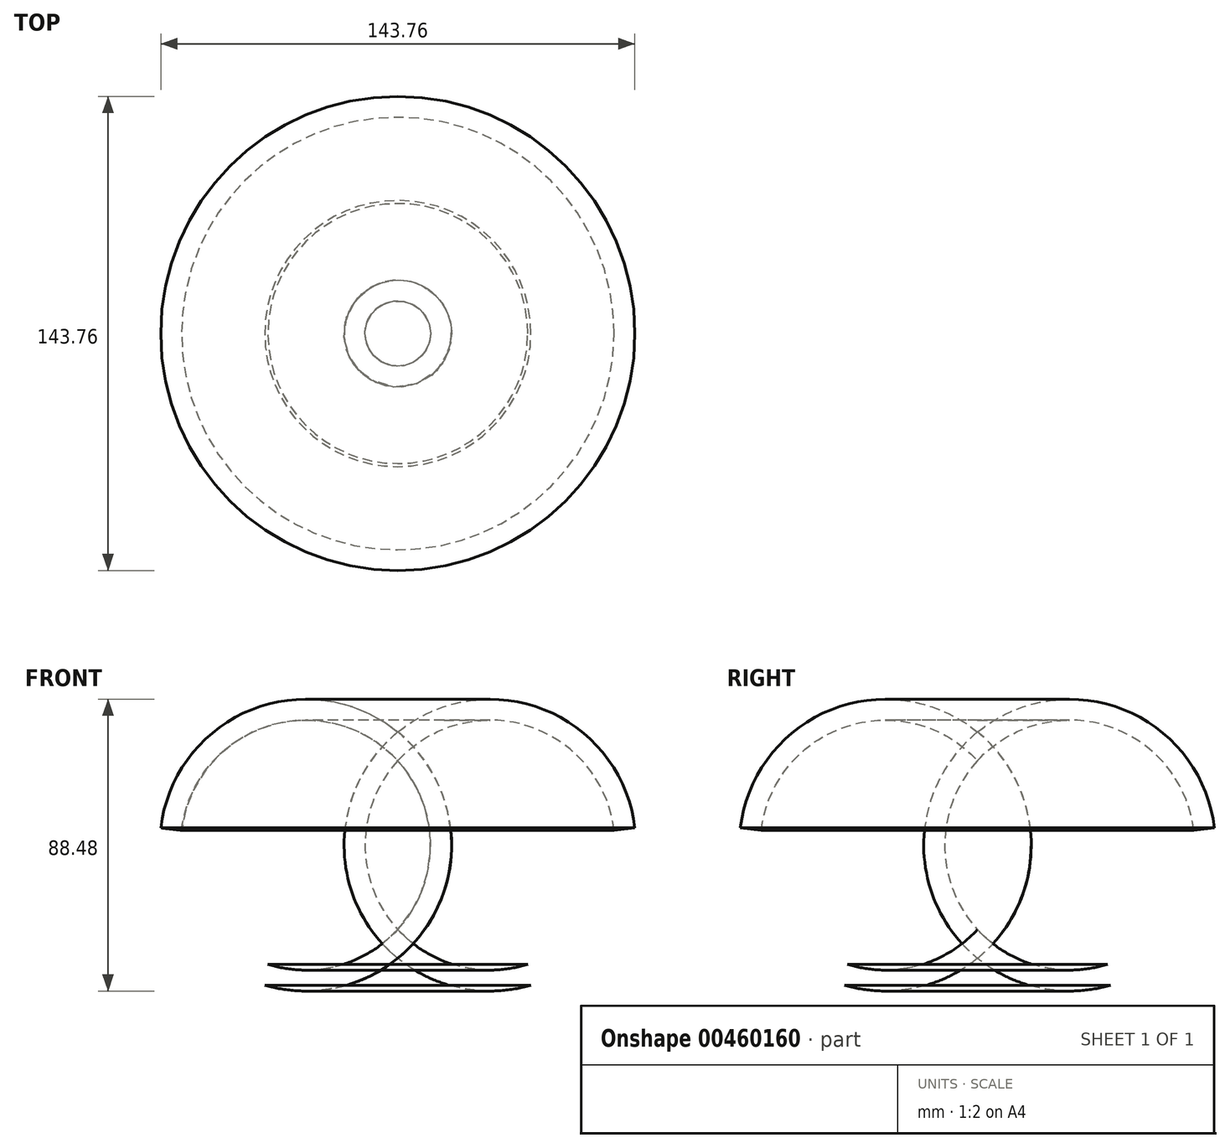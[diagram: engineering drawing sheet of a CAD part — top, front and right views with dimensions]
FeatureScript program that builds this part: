
annotation { "Feature Type Name" : "Feature", "Feature Type Description" : "" }
export const myFeature = defineFeature(function(context is Context, id is Id, definition is map)
    precondition{}
    {
        {
            var Q0;
            Q0=qCreatedBy(makeId("Front.planeOp"),FACE);
            var sketch = newSketch(context, id + "F0", { "sketchPlane" : qUnion([Q0])});
            skLineSegment(sketch, "E0", {"start": v(0, 0) * mm, "end": v(0, 75.5) * mm, "construction": true});
            skArc(sketch, "E1", {"start": v(39.4, 0) * mm, "mid": v(59.8, 15.6) * mm, "end": v(65.57, 40.6) * mm});
            skLineSegment(sketch, "E2", {"start": v(0, 0) * mm, "end": v(39.4, 0) * mm});
            skArc(sketch, "E3.0", {"start": v(40.35, -6.35) * mm, "mid": v(64.86, 11.73) * mm, "end": v(71.88, 41.36) * mm});
            skLineSegment(sketch, "E3.1", {"start": v(0, -6.35) * mm, "end": v(40.35, -6.35) * mm});
            skLineSegment(sketch, "E4", {"start": v(65.57, 40.6) * mm, "end": v(71.88, 41.36) * mm});
            skLineSegment(sketch, "E5", {"start": v(0, 0) * mm, "end": v(0, -6.35) * mm});
            skSolve(sketch);
        }
        {
            var Q0;
            Q0=makeQuery(id+"F0.imprint","IMPRINT",FACE,{"disambiguationData":[TD([[makeQuery(id+"F0.imprint","IMPRINT",EDGE,{"derivedFrom":sQuery(id+"F0.wireOp",EDGE,"E1")}),-1.0]])]});
            var Q1;
            Q1=sQuery(id+"F0.wireOp",EDGE,"E0");
            revolve(context, id + "F1", {"entities" : qUnion([Q0]), "axis" : qUnion([Q1]), "revolveType" : RevolveType.FULL});
        }
        {
            var Q0;
            Q0=qCreatedBy(makeId("Front.planeOp"),FACE);
            var sketch = newSketch(context, id + "F2", { "sketchPlane" : qUnion([Q0])});
            skLineSegment(sketch, "E6", {"start": v(60.76, 11.13) * mm, "end": v(69.48, 8.42) * mm});
            skLineSegment(sketch, "E7", {"start": v(69.48, 8.42) * mm, "end": v(72.19, 0) * mm});
            skLineSegment(sketch, "E8", {"start": v(72.19, 0) * mm, "end": v(72.19, -10.23) * mm});
            skLineSegment(sketch, "E9", {"start": v(72.19, -10.23) * mm, "end": v(72.19, -17.75) * mm});
            skLineSegment(sketch, "E10", {"start": v(72.19, -17.75) * mm, "end": v(46.92, 0) * mm});
            skArc(sketch, "E11", {"start": v(46.92, 0) * mm, "mid": v(55.46, 3.56) * mm, "end": v(60.76, 11.13) * mm});
            skSolve(sketch);
        }
        {
            var Q0;
            Q0 = qSketchRegion(id + "F2", true);
            extrude(context, id + "F3", {"entities" : qUnion([Q0]), "operationType" : NewBodyOperationType.ADD, "depth" : 2.54 * mm});
        }
        {
            var Q0;
            Q0=makeQuery(id+"F1.opRevolve","SWEPT_BODY",BODY,{"disambiguationData":[OSD([sQuery(id+"F0.wireOp",EDGE,"E1"),sQuery(id+"F0.wireOp",EDGE,"E2"),sQuery(id+"F0.wireOp",EDGE,"E3.0"),sQuery(id+"F0.wireOp",EDGE,"E3.1"),sQuery(id+"F0.wireOp",EDGE,"E4"),sQuery(id+"F0.wireOp",EDGE,"E5")])]});
            var Q1;
            Q1=makeQuery(id+"F1.opRevolve","SWEPT_EDGE",EDGE,{"disambiguationData":[OSD([sQuery(id+"F0.wireOp",EDGE,"E3.0"),sQuery(id+"F0.wireOp",EDGE,"E4")])]});
            circularPattern(context, id + "F4", {"entities" : qUnion([Q0]), "axis" : qUnion([Q1]), "angle" : 360 * degree, "instanceCount" : 3, "equalSpace" : true});
        }
    });
